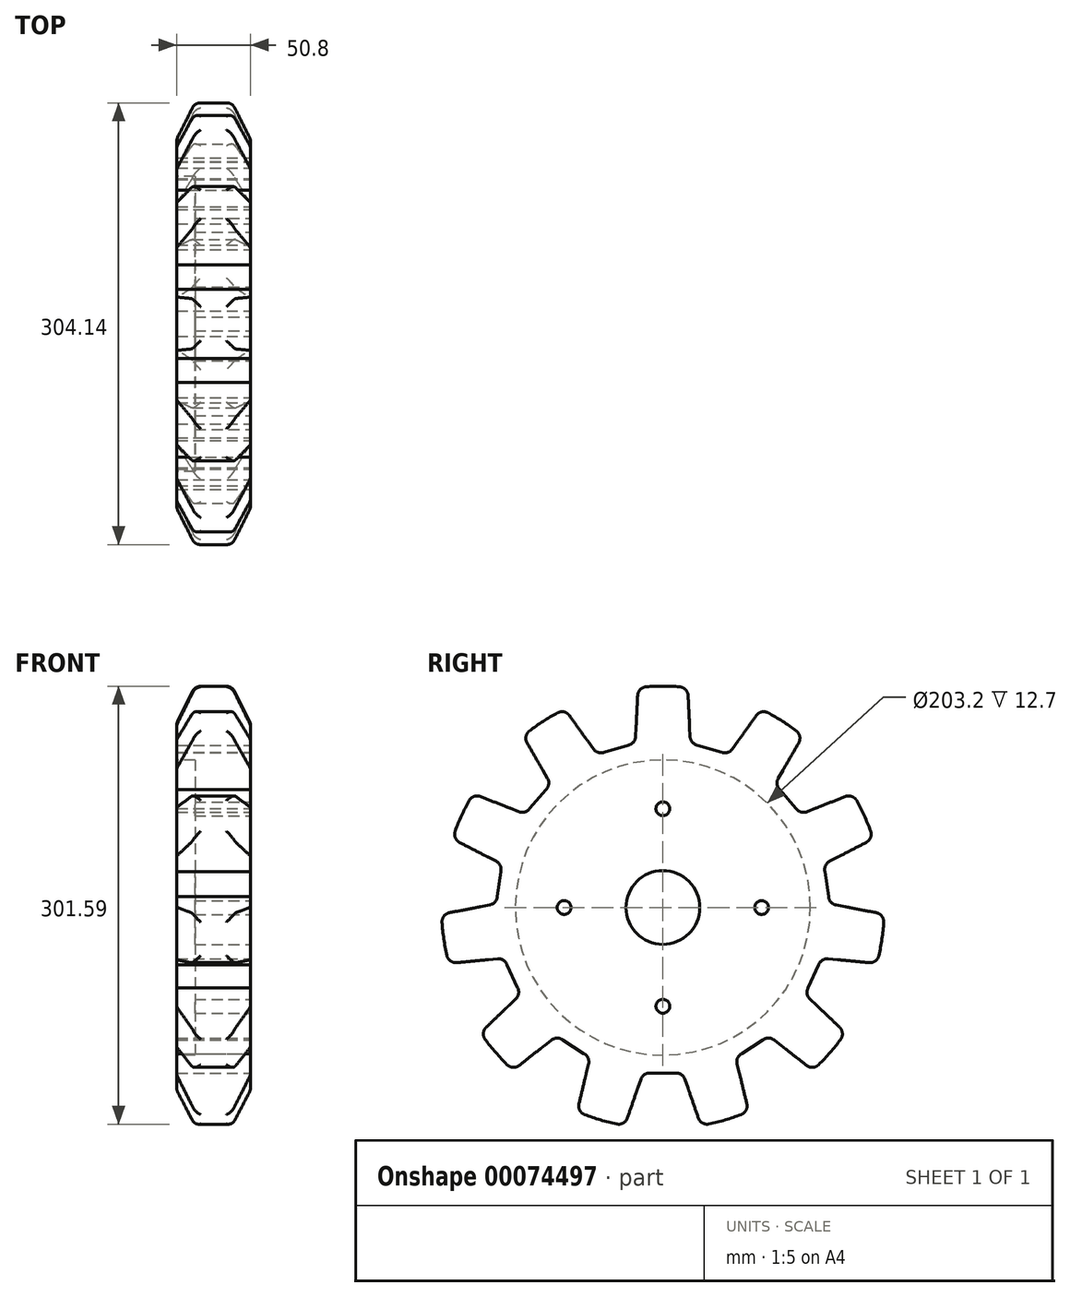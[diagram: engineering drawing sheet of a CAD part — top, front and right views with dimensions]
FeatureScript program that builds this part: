
annotation { "Feature Type Name" : "Feature", "Feature Type Description" : "" }
export const myFeature = defineFeature(function(context is Context, id is Id, definition is map)
    precondition{}
    {
        {
            var Q0;
            Q0=qCreatedBy(makeId("Front.planeOp"),FACE);
            var sketch = newSketch(context, id + "F0", { "sketchPlane" : qUnion([Q0])});
            skLineSegment(sketch, "E0.bottom", {"start": v(0, 0) * mm, "end": v(50.8, 0) * mm});
            skLineSegment(sketch, "E0.top", {"start": v(16.62, 152.4) * mm, "end": v(34.18, 152.4) * mm});
            skLineSegment(sketch, "E0.left", {"start": v(0, 0) * mm, "end": v(0, 125.5) * mm});
            skLineSegment(sketch, "E0.right", {"start": v(50.8, 0) * mm, "end": v(50.8, 125.5) * mm});
            skLineSegment(sketch, "E1", {"start": v(0.67, 128.34) * mm, "end": v(10.94, 148.89) * mm});
            skLineSegment(sketch, "E2", {"start": v(50.13, 128.34) * mm, "end": v(39.86, 148.89) * mm});
            skPoint(sketch, "E3.orphan", {"position": v(0, 152.4) * mm});
            skPoint(sketch, "E4.orphan", {"position": v(50.8, 152.4) * mm});
            skPoint(sketch, "E5.visualSharp", {"position": v(12.7, 152.4) * mm});
            skArc(sketch, "E5.filletArc", {"start": v(16.62, 152.4) * mm, "mid": v(13.29, 151.45) * mm, "end": v(10.94, 148.89) * mm});
            skPoint(sketch, "E6.visualSharp", {"position": v(38.1, 152.4) * mm});
            skArc(sketch, "E6.filletArc", {"start": v(39.86, 148.89) * mm, "mid": v(37.51, 151.45) * mm, "end": v(34.18, 152.4) * mm});
            skPoint(sketch, "E7.visualSharp", {"position": v(50.8, 127) * mm});
            skArc(sketch, "E7.filletArc", {"start": v(50.8, 125.5) * mm, "mid": v(50.63, 126.96) * mm, "end": v(50.13, 128.34) * mm});
            skPoint(sketch, "E8.visualSharp", {"position": v(0, 127) * mm});
            skArc(sketch, "E8.filletArc", {"start": v(0.67, 128.34) * mm, "mid": v(0.17, 126.96) * mm, "end": v(0, 125.5) * mm});
            skSolve(sketch);
        }
        {
            var Q0;
            Q0=makeQuery(id+"F0.imprint","IMPRINT",FACE,{"disambiguationData":[TD([[makeQuery(id+"F0.imprint","IMPRINT",EDGE,{"derivedFrom":sQuery(id+"F0.wireOp",EDGE,"E0.bottom")}),1.0]])]});
            var Q1;
            Q1=sQuery(id+"F0.wireOp",EDGE,"E0.bottom");
            revolve(context, id + "F1", {"surfaceOperationType" : NewSurfaceOperationType.NEW, "entities" : qUnion([Q0]), "axis" : qUnion([Q1]), "revolveType" : RevolveType.FULL});
        }
        {
            var Q0;
            Q0=makeQuery(id+"F1.opRevolve","SWEPT_FACE",FACE,{"disambiguationData":[OSD([sQuery(id+"F0.wireOp",EDGE,"E0.right")])]});
            var sketch = newSketch(context, id + "F2", { "sketchPlane" : qUnion([Q0])});
            skArc(sketch, "E9", {"start": v(11.52, 151.96) * mm, "mid": v(0, 152.4) * mm, "end": v(-11.52, 151.96) * mm});
            skLineSegment(sketch, "E10", {"start": v(0, 114.3) * mm, "end": v(0, 152.4) * mm});
            skLineSegment(sketch, "E11", {"start": v(18.74, 117.7) * mm, "end": v(17.38, 145.94) * mm});
            skLineSegment(sketch, "E12", {"start": v(-18.74, 117.7) * mm, "end": v(-17.38, 145.94) * mm});
            skPoint(sketch, "E13.visualSharp", {"position": v(-17.12, 151.44) * mm});
            skArc(sketch, "E13.filletArc", {"start": v(-11.52, 151.96) * mm, "mid": v(-15.6, 150.06) * mm, "end": v(-17.38, 145.94) * mm});
            skPoint(sketch, "E14.visualSharp", {"position": v(17.12, 151.44) * mm});
            skArc(sketch, "E14.filletArc", {"start": v(17.38, 145.94) * mm, "mid": v(15.6, 150.06) * mm, "end": v(11.52, 151.96) * mm});
            skPoint(sketch, "E15.visualSharp", {"position": v(18.98, 112.71) * mm});
            skArc(sketch, "E15.filletArc", {"start": v(18.74, 117.7) * mm, "mid": v(20.25, 113.9) * mm, "end": v(23.77, 111.8) * mm});
            skPoint(sketch, "E16.visualSharp", {"position": v(-18.98, 112.71) * mm});
            skArc(sketch, "E16.filletArc", {"start": v(-23.77, 111.8) * mm, "mid": v(-20.25, 113.9) * mm, "end": v(-18.74, 117.7) * mm});
            skLineSegment(sketch, "E17.1.0", {"start": v(47.87, 109.16) * mm, "end": v(64.28, 132.17) * mm});
            skArc(sketch, "E17.1.1", {"start": v(72.47, 134.07) * mm, "mid": v(68.01, 134.67) * mm, "end": v(64.28, 132.17) * mm});
            skArc(sketch, "E17.1.2", {"start": v(91.85, 121.61) * mm, "mid": v(82.4, 128.2) * mm, "end": v(72.47, 134.07) * mm});
            skArc(sketch, "E17.1.3", {"start": v(93.52, 113.37) * mm, "mid": v(94.25, 117.8) * mm, "end": v(91.85, 121.61) * mm});
            skLineSegment(sketch, "E17.1.4", {"start": v(79.4, 88.89) * mm, "end": v(93.52, 113.37) * mm});
            skArc(sketch, "E17.1.5", {"start": v(79.4, 88.89) * mm, "mid": v(78.61, 84.87) * mm, "end": v(80.44, 81.2) * mm});
            skArc(sketch, "E17.1.6", {"start": v(40.45, 106.9) * mm, "mid": v(44.54, 106.77) * mm, "end": v(47.87, 109.16) * mm});
            skLineSegment(sketch, "E17.2.0", {"start": v(99.28, 65.95) * mm, "end": v(125.53, 76.44) * mm});
            skArc(sketch, "E17.2.1", {"start": v(133.45, 73.6) * mm, "mid": v(130.02, 76.52) * mm, "end": v(125.53, 76.44) * mm});
            skArc(sketch, "E17.2.2", {"start": v(143.02, 52.65) * mm, "mid": v(138.63, 63.3) * mm, "end": v(133.45, 73.6) * mm});
            skArc(sketch, "E17.2.3", {"start": v(139.97, 44.81) * mm, "mid": v(142.98, 48.15) * mm, "end": v(143.02, 52.65) * mm});
            skLineSegment(sketch, "E17.2.4", {"start": v(114.86, 31.85) * mm, "end": v(139.97, 44.81) * mm});
            skArc(sketch, "E17.2.5", {"start": v(114.86, 31.85) * mm, "mid": v(112.02, 28.9) * mm, "end": v(111.57, 24.83) * mm});
            skArc(sketch, "E17.2.6", {"start": v(91.83, 68.06) * mm, "mid": v(95.2, 65.73) * mm, "end": v(99.28, 65.95) * mm});
            skLineSegment(sketch, "E17.3.0", {"start": v(119.18, 1.8) * mm, "end": v(146.93, -3.56) * mm});
            skArc(sketch, "E17.3.1", {"start": v(152.06, -10.22) * mm, "mid": v(150.75, -5.92) * mm, "end": v(146.93, -3.56) * mm});
            skArc(sketch, "E17.3.2", {"start": v(148.78, -33.03) * mm, "mid": v(150.85, -21.69) * mm, "end": v(152.06, -10.22) * mm});
            skArc(sketch, "E17.3.3", {"start": v(141.98, -37.97) * mm, "mid": v(146.31, -36.79) * mm, "end": v(148.78, -33.03) * mm});
            skLineSegment(sketch, "E17.3.4", {"start": v(113.84, -35.3) * mm, "end": v(141.98, -37.97) * mm});
            skArc(sketch, "E17.3.5", {"start": v(113.84, -35.3) * mm, "mid": v(109.86, -36.25) * mm, "end": v(107.28, -39.43) * mm});
            skArc(sketch, "E17.3.6", {"start": v(114.05, 7.61) * mm, "mid": v(115.62, 3.83) * mm, "end": v(119.18, 1.8) * mm});
            skLineSegment(sketch, "E17.4.0", {"start": v(101.23, -62.92) * mm, "end": v(121.68, -82.43) * mm});
            skArc(sketch, "E17.4.1", {"start": v(122.4, -90.8) * mm, "mid": v(123.62, -86.49) * mm, "end": v(121.68, -82.43) * mm});
            skArc(sketch, "E17.4.2", {"start": v(107.3, -108.22) * mm, "mid": v(115.18, -99.8) * mm, "end": v(122.4, -90.8) * mm});
            skArc(sketch, "E17.4.3", {"start": v(98.9, -108.7) * mm, "mid": v(103.2, -110.05) * mm, "end": v(107.3, -108.22) * mm});
            skLineSegment(sketch, "E17.4.4", {"start": v(76.68, -91.25) * mm, "end": v(98.9, -108.7) * mm});
            skArc(sketch, "E17.4.5", {"start": v(76.68, -91.25) * mm, "mid": v(72.82, -89.9) * mm, "end": v(68.93, -91.18) * mm});
            skArc(sketch, "E17.4.6", {"start": v(100.06, -55.25) * mm, "mid": v(99.34, -59.29) * mm, "end": v(101.23, -62.92) * mm});
            skLineSegment(sketch, "E17.5.0", {"start": v(51.15, -107.66) * mm, "end": v(57.8, -135.13) * mm});
            skArc(sketch, "E17.5.1", {"start": v(53.87, -142.56) * mm, "mid": v(57.24, -139.59) * mm, "end": v(57.8, -135.13) * mm});
            skArc(sketch, "E17.5.2", {"start": v(31.76, -149.05) * mm, "mid": v(42.94, -146.23) * mm, "end": v(53.87, -142.56) * mm});
            skArc(sketch, "E17.5.3", {"start": v(24.44, -144.92) * mm, "mid": v(27.32, -148.37) * mm, "end": v(31.76, -149.05) * mm});
            skLineSegment(sketch, "E17.5.4", {"start": v(15.18, -118.22) * mm, "end": v(24.44, -144.92) * mm});
            skArc(sketch, "E17.5.5", {"start": v(15.18, -118.22) * mm, "mid": v(12.66, -115) * mm, "end": v(8.7, -113.97) * mm});
            skArc(sketch, "E17.5.6", {"start": v(54.3, -100.58) * mm, "mid": v(51.52, -103.58) * mm, "end": v(51.15, -107.66) * mm});
            skLineSegment(sketch, "E17.6.0", {"start": v(-15.18, -118.22) * mm, "end": v(-24.44, -144.92) * mm});
            skArc(sketch, "E17.6.1", {"start": v(-31.76, -149.05) * mm, "mid": v(-27.32, -148.37) * mm, "end": v(-24.44, -144.92) * mm});
            skArc(sketch, "E17.6.2", {"start": v(-53.87, -142.56) * mm, "mid": v(-42.94, -146.23) * mm, "end": v(-31.76, -149.05) * mm});
            skArc(sketch, "E17.6.3", {"start": v(-57.8, -135.13) * mm, "mid": v(-57.24, -139.59) * mm, "end": v(-53.87, -142.56) * mm});
            skLineSegment(sketch, "E17.6.4", {"start": v(-51.15, -107.66) * mm, "end": v(-57.8, -135.13) * mm});
            skArc(sketch, "E17.6.5", {"start": v(-51.15, -107.66) * mm, "mid": v(-51.52, -103.58) * mm, "end": v(-54.3, -100.58) * mm});
            skArc(sketch, "E17.6.6", {"start": v(-8.7, -113.97) * mm, "mid": v(-12.66, -115) * mm, "end": v(-15.18, -118.22) * mm});
            skLineSegment(sketch, "E17.7.0", {"start": v(-76.68, -91.25) * mm, "end": v(-98.9, -108.7) * mm});
            skArc(sketch, "E17.7.1", {"start": v(-107.3, -108.22) * mm, "mid": v(-103.2, -110.05) * mm, "end": v(-98.9, -108.7) * mm});
            skArc(sketch, "E17.7.2", {"start": v(-122.4, -90.8) * mm, "mid": v(-115.18, -99.8) * mm, "end": v(-107.3, -108.22) * mm});
            skArc(sketch, "E17.7.3", {"start": v(-121.68, -82.43) * mm, "mid": v(-123.62, -86.49) * mm, "end": v(-122.4, -90.8) * mm});
            skLineSegment(sketch, "E17.7.4", {"start": v(-101.23, -62.92) * mm, "end": v(-121.68, -82.43) * mm});
            skArc(sketch, "E17.7.5", {"start": v(-101.23, -62.92) * mm, "mid": v(-99.34, -59.29) * mm, "end": v(-100.06, -55.25) * mm});
            skArc(sketch, "E17.7.6", {"start": v(-68.93, -91.18) * mm, "mid": v(-72.82, -89.9) * mm, "end": v(-76.68, -91.25) * mm});
            skLineSegment(sketch, "E17.8.0", {"start": v(-113.84, -35.3) * mm, "end": v(-141.98, -37.97) * mm});
            skArc(sketch, "E17.8.1", {"start": v(-148.78, -33.03) * mm, "mid": v(-146.31, -36.79) * mm, "end": v(-141.98, -37.97) * mm});
            skArc(sketch, "E17.8.2", {"start": v(-152.06, -10.22) * mm, "mid": v(-150.85, -21.69) * mm, "end": v(-148.78, -33.03) * mm});
            skArc(sketch, "E17.8.3", {"start": v(-146.93, -3.56) * mm, "mid": v(-150.75, -5.92) * mm, "end": v(-152.06, -10.22) * mm});
            skLineSegment(sketch, "E17.8.4", {"start": v(-119.18, 1.8) * mm, "end": v(-146.93, -3.56) * mm});
            skArc(sketch, "E17.8.5", {"start": v(-119.18, 1.8) * mm, "mid": v(-115.62, 3.83) * mm, "end": v(-114.05, 7.61) * mm});
            skArc(sketch, "E17.8.6", {"start": v(-107.28, -39.43) * mm, "mid": v(-109.86, -36.25) * mm, "end": v(-113.84, -35.3) * mm});
            skLineSegment(sketch, "E17.9.0", {"start": v(-114.86, 31.85) * mm, "end": v(-139.97, 44.81) * mm});
            skArc(sketch, "E17.9.1", {"start": v(-143.02, 52.65) * mm, "mid": v(-142.98, 48.15) * mm, "end": v(-139.97, 44.81) * mm});
            skArc(sketch, "E17.9.2", {"start": v(-133.45, 73.6) * mm, "mid": v(-138.63, 63.3) * mm, "end": v(-143.02, 52.65) * mm});
            skArc(sketch, "E17.9.3", {"start": v(-125.53, 76.44) * mm, "mid": v(-130.02, 76.52) * mm, "end": v(-133.45, 73.6) * mm});
            skLineSegment(sketch, "E17.9.4", {"start": v(-99.28, 65.95) * mm, "end": v(-125.53, 76.44) * mm});
            skArc(sketch, "E17.9.5", {"start": v(-99.28, 65.95) * mm, "mid": v(-95.2, 65.73) * mm, "end": v(-91.83, 68.06) * mm});
            skArc(sketch, "E17.9.6", {"start": v(-111.57, 24.83) * mm, "mid": v(-112.02, 28.9) * mm, "end": v(-114.86, 31.85) * mm});
            skLineSegment(sketch, "E17.10.0", {"start": v(-79.4, 88.89) * mm, "end": v(-93.52, 113.37) * mm});
            skArc(sketch, "E17.10.1", {"start": v(-91.85, 121.61) * mm, "mid": v(-94.25, 117.8) * mm, "end": v(-93.52, 113.37) * mm});
            skArc(sketch, "E17.10.2", {"start": v(-72.47, 134.07) * mm, "mid": v(-82.4, 128.2) * mm, "end": v(-91.85, 121.61) * mm});
            skArc(sketch, "E17.10.3", {"start": v(-64.28, 132.17) * mm, "mid": v(-68.01, 134.67) * mm, "end": v(-72.47, 134.07) * mm});
            skLineSegment(sketch, "E17.10.4", {"start": v(-47.87, 109.16) * mm, "end": v(-64.28, 132.17) * mm});
            skArc(sketch, "E17.10.5", {"start": v(-47.87, 109.16) * mm, "mid": v(-44.54, 106.77) * mm, "end": v(-40.45, 106.9) * mm});
            skArc(sketch, "E17.10.6", {"start": v(-80.44, 81.2) * mm, "mid": v(-78.61, 84.87) * mm, "end": v(-79.4, 88.89) * mm});
            skLineSegment(sketch, "E17.anchor1", {"start": v(0, 0) * mm, "end": v(-18.74, 117.7) * mm, "construction": true});
            skLineSegment(sketch, "E17.anchor2", {"start": v(0, 0) * mm, "end": v(-79.4, 88.89) * mm, "construction": true});
            skLineSegment(sketch, "E18", {"start": v(-114.05, 7.61) * mm, "end": v(-111.57, 24.83) * mm});
            skLineSegment(sketch, "E19", {"start": v(-91.83, 68.06) * mm, "end": v(-80.44, 81.2) * mm});
            skLineSegment(sketch, "E20", {"start": v(-40.45, 106.9) * mm, "end": v(-23.77, 111.8) * mm});
            skLineSegment(sketch, "E21", {"start": v(23.77, 111.8) * mm, "end": v(40.45, 106.9) * mm});
            skLineSegment(sketch, "E22", {"start": v(80.44, 81.2) * mm, "end": v(91.83, 68.06) * mm});
            skLineSegment(sketch, "E23", {"start": v(111.57, 24.83) * mm, "end": v(114.05, 7.61) * mm});
            skLineSegment(sketch, "E24", {"start": v(107.28, -39.43) * mm, "end": v(100.06, -55.25) * mm});
            skLineSegment(sketch, "E25", {"start": v(68.93, -91.18) * mm, "end": v(54.3, -100.58) * mm});
            skLineSegment(sketch, "E26", {"start": v(8.7, -113.97) * mm, "end": v(-8.7, -113.97) * mm});
            skLineSegment(sketch, "E27", {"start": v(-54.3, -100.58) * mm, "end": v(-68.93, -91.18) * mm});
            skLineSegment(sketch, "E28", {"start": v(-100.06, -55.25) * mm, "end": v(-107.28, -39.43) * mm});
            skCircle(sketch, "E29", {"center": v(0, 0) * mm, "radius": 152.4 * mm});
            skSolve(sketch);
        }
        {
            var Q0;
            {var subQ5=sQuery(id+"F2.wireOp",EDGE,"E17.8.3");Q0=makeQuery(id+"F2.imprint","IMPRINT",FACE,{"disambiguationData":[TD([[makeQuery(id+"F2.imprint","IMPRINT",EDGE,{"derivedFrom":subQ5}),-1.0]])]});}
            var Q1;
            {var subQ4=sQuery(id+"F2.wireOp",EDGE,"E17.8.5");Q1=makeQuery(id+"F2.imprint","IMPRINT",FACE,{"disambiguationData":[TD([[makeQuery(id+"F2.imprint","IMPRINT",EDGE,{"derivedFrom":subQ4}),1.0]])]});}
            var Q2;
            {var subQ6=sQuery(id+"F2.wireOp",EDGE,"E17.9.5");Q2=makeQuery(id+"F2.imprint","IMPRINT",FACE,{"disambiguationData":[TD([[makeQuery(id+"F2.imprint","IMPRINT",EDGE,{"derivedFrom":subQ6}),1.0]])]});}
            var Q3;
            {var subQ5=sQuery(id+"F2.wireOp",EDGE,"E17.9.3");Q3=makeQuery(id+"F2.imprint","IMPRINT",FACE,{"disambiguationData":[TD([[makeQuery(id+"F2.imprint","IMPRINT",EDGE,{"derivedFrom":subQ5}),-1.0]])]});}
            var Q4;
            {var subQ4=sQuery(id+"F2.wireOp",EDGE,"E16.filletArc");Q4=makeQuery(id+"F2.imprint","IMPRINT",FACE,{"disambiguationData":[TD([[makeQuery(id+"F2.imprint","IMPRINT",EDGE,{"derivedFrom":subQ4}),1.0]])]});}
            var Q5;
            {var subQ4=sQuery(id+"F2.wireOp",EDGE,"E13.filletArc");Q5=makeQuery(id+"F2.imprint","IMPRINT",FACE,{"disambiguationData":[TD([[makeQuery(id+"F2.imprint","IMPRINT",EDGE,{"derivedFrom":subQ4}),-1.0]])]});}
            var Q6;
            {var subQ4=sQuery(id+"F2.wireOp",EDGE,"E14.filletArc");Q6=makeQuery(id+"F2.imprint","IMPRINT",FACE,{"disambiguationData":[TD([[makeQuery(id+"F2.imprint","IMPRINT",EDGE,{"derivedFrom":subQ4}),-1.0]])]});}
            var Q7;
            {var subQ4=sQuery(id+"F2.wireOp",EDGE,"E15.filletArc");Q7=makeQuery(id+"F2.imprint","IMPRINT",FACE,{"disambiguationData":[TD([[makeQuery(id+"F2.imprint","IMPRINT",EDGE,{"derivedFrom":subQ4}),1.0]])]});}
            var Q8;
            {var subQ5=sQuery(id+"F2.wireOp",EDGE,"E17.1.3");Q8=makeQuery(id+"F2.imprint","IMPRINT",FACE,{"disambiguationData":[TD([[makeQuery(id+"F2.imprint","IMPRINT",EDGE,{"derivedFrom":subQ5}),-1.0]])]});}
            var Q9;
            {var subQ4=sQuery(id+"F2.wireOp",EDGE,"E17.1.5");Q9=makeQuery(id+"F2.imprint","IMPRINT",FACE,{"disambiguationData":[TD([[makeQuery(id+"F2.imprint","IMPRINT",EDGE,{"derivedFrom":subQ4}),1.0]])]});}
            var Q10;
            {var subQ6=sQuery(id+"F2.wireOp",EDGE,"E17.2.3");Q10=makeQuery(id+"F2.imprint","IMPRINT",FACE,{"disambiguationData":[TD([[makeQuery(id+"F2.imprint","IMPRINT",EDGE,{"derivedFrom":subQ6}),-1.0]])]});}
            var Q11;
            {var subQ4=sQuery(id+"F2.wireOp",EDGE,"E17.2.5");Q11=makeQuery(id+"F2.imprint","IMPRINT",FACE,{"disambiguationData":[TD([[makeQuery(id+"F2.imprint","IMPRINT",EDGE,{"derivedFrom":subQ4}),1.0]])]});}
            var Q12;
            {var subQ5=sQuery(id+"F2.wireOp",EDGE,"E17.3.3");Q12=makeQuery(id+"F2.imprint","IMPRINT",FACE,{"disambiguationData":[TD([[makeQuery(id+"F2.imprint","IMPRINT",EDGE,{"derivedFrom":subQ5}),-1.0]])]});}
            var Q13;
            {var subQ4=sQuery(id+"F2.wireOp",EDGE,"E17.3.5");Q13=makeQuery(id+"F2.imprint","IMPRINT",FACE,{"disambiguationData":[TD([[makeQuery(id+"F2.imprint","IMPRINT",EDGE,{"derivedFrom":subQ4}),1.0]])]});}
            var Q14;
            {var subQ5=sQuery(id+"F2.wireOp",EDGE,"E17.4.3");Q14=makeQuery(id+"F2.imprint","IMPRINT",FACE,{"disambiguationData":[TD([[makeQuery(id+"F2.imprint","IMPRINT",EDGE,{"derivedFrom":subQ5}),-1.0]])]});}
            var Q15;
            {var subQ4=sQuery(id+"F2.wireOp",EDGE,"E17.4.5");Q15=makeQuery(id+"F2.imprint","IMPRINT",FACE,{"disambiguationData":[TD([[makeQuery(id+"F2.imprint","IMPRINT",EDGE,{"derivedFrom":subQ4}),1.0]])]});}
            var Q16;
            {var subQ5=sQuery(id+"F2.wireOp",EDGE,"E17.5.3");Q16=makeQuery(id+"F2.imprint","IMPRINT",FACE,{"disambiguationData":[TD([[makeQuery(id+"F2.imprint","IMPRINT",EDGE,{"derivedFrom":subQ5}),-1.0]])]});}
            var Q17;
            {var subQ4=sQuery(id+"F2.wireOp",EDGE,"E17.5.5");Q17=makeQuery(id+"F2.imprint","IMPRINT",FACE,{"disambiguationData":[TD([[makeQuery(id+"F2.imprint","IMPRINT",EDGE,{"derivedFrom":subQ4}),1.0]])]});}
            var Q18;
            {var subQ5=sQuery(id+"F2.wireOp",EDGE,"E17.6.3");Q18=makeQuery(id+"F2.imprint","IMPRINT",FACE,{"disambiguationData":[TD([[makeQuery(id+"F2.imprint","IMPRINT",EDGE,{"derivedFrom":subQ5}),-1.0]])]});}
            var Q19;
            {var subQ4=sQuery(id+"F2.wireOp",EDGE,"E17.6.5");Q19=makeQuery(id+"F2.imprint","IMPRINT",FACE,{"disambiguationData":[TD([[makeQuery(id+"F2.imprint","IMPRINT",EDGE,{"derivedFrom":subQ4}),1.0]])]});}
            var Q20;
            {var subQ5=sQuery(id+"F2.wireOp",EDGE,"E17.7.3");Q20=makeQuery(id+"F2.imprint","IMPRINT",FACE,{"disambiguationData":[TD([[makeQuery(id+"F2.imprint","IMPRINT",EDGE,{"derivedFrom":subQ5}),-1.0]])]});}
            var Q21;
            {var subQ6=sQuery(id+"F2.wireOp",EDGE,"E17.7.5");Q21=makeQuery(id+"F2.imprint","IMPRINT",FACE,{"disambiguationData":[TD([[makeQuery(id+"F2.imprint","IMPRINT",EDGE,{"derivedFrom":subQ6}),1.0]])]});}
            extrude(context, id + "F3", {"entities" : qUnion([Q0, Q1, Q2, Q3, Q4, Q5, Q6, Q7, Q8, Q9, Q10, Q11, Q12, Q13, Q14, Q15, Q16, Q17, Q18, Q19, Q20, Q21]), "operationType" : NewBodyOperationType.REMOVE, "oppositeDirection" : true, "depth" : 50.8 * mm, "offsetDistance" : 25.4 * mm});
        }
        {
            var Q0;
            Q0=makeQuery(id+"F1.opRevolve","SWEPT_FACE",FACE,{"disambiguationData":[OSD([sQuery(id+"F0.wireOp",EDGE,"E0.right")])]});
            var sketch = newSketch(context, id + "F4", { "sketchPlane" : qUnion([Q0])});
            skCircle(sketch, "E30", {"center": v(0, 68) * mm, "radius": 4.76 * mm});
            skCircle(sketch, "E31", {"center": v(0, 0) * mm, "radius": 25.4 * mm});
            skCircle(sketch, "E32.1.0", {"center": v(-68, 0) * mm, "radius": 4.76 * mm});
            skCircle(sketch, "E32.2.0", {"center": v(0, -68) * mm, "radius": 4.76 * mm});
            skCircle(sketch, "E32.3.0", {"center": v(68, 0) * mm, "radius": 4.76 * mm});
            skSolve(sketch);
        }
        {
            var Q0;
            Q0=makeQuery(id+"F4.imprint","IMPRINT",FACE,{"disambiguationData":[TD([[makeQuery(id+"F4.imprint","IMPRINT",EDGE,{"derivedFrom":sQuery(id+"F4.wireOp",EDGE,"E30")}),1.0]])]});
            var Q1;
            Q1=makeQuery(id+"F4.imprint","IMPRINT",FACE,{"disambiguationData":[TD([[makeQuery(id+"F4.imprint","IMPRINT",EDGE,{"derivedFrom":sQuery(id+"F4.wireOp",EDGE,"E32.1.0")}),1.0]])]});
            var Q2;
            Q2=makeQuery(id+"F4.imprint","IMPRINT",FACE,{"disambiguationData":[TD([[makeQuery(id+"F4.imprint","IMPRINT",EDGE,{"derivedFrom":sQuery(id+"F4.wireOp",EDGE,"E31")}),1.0]])]});
            var Q3;
            Q3=makeQuery(id+"F4.imprint","IMPRINT",FACE,{"disambiguationData":[TD([[makeQuery(id+"F4.imprint","IMPRINT",EDGE,{"derivedFrom":sQuery(id+"F4.wireOp",EDGE,"E32.2.0")}),1.0]])]});
            var Q4;
            Q4=makeQuery(id+"F4.imprint","IMPRINT",FACE,{"disambiguationData":[TD([[makeQuery(id+"F4.imprint","IMPRINT",EDGE,{"derivedFrom":sQuery(id+"F4.wireOp",EDGE,"E32.3.0")}),1.0]])]});
            extrude(context, id + "F5", {"entities" : qUnion([Q0, Q1, Q2, Q3, Q4]), "operationType" : NewBodyOperationType.REMOVE, "oppositeDirection" : true, "depth" : 50.8 * mm, "offsetDistance" : 25.4 * mm});
        }
        {
            var Q0;
            Q0=makeQuery(id+"F1.opRevolve","SWEPT_FACE",FACE,{"disambiguationData":[OSD([sQuery(id+"F0.wireOp",EDGE,"E0.left")])]});
            var sketch = newSketch(context, id + "F6", { "sketchPlane" : qUnion([Q0])});
            skCircle(sketch, "E33", {"center": v(0, 0) * mm, "radius": 101.6 * mm});
            skSolve(sketch);
        }
        {
            var Q0;
            Q0=makeQuery(id+"F6.imprint","IMPRINT",FACE,{"disambiguationData":[TD([[makeQuery(id+"F6.imprint","IMPRINT",EDGE,{"derivedFrom":sQuery(id+"F6.wireOp",EDGE,"E33")}),1.0]])]});
            extrude(context, id + "F7", {"entities" : qUnion([Q0]), "operationType" : NewBodyOperationType.REMOVE, "oppositeDirection" : true, "depth" : 12.7 * mm, "offsetDistance" : 25.4 * mm});
        }
    });
